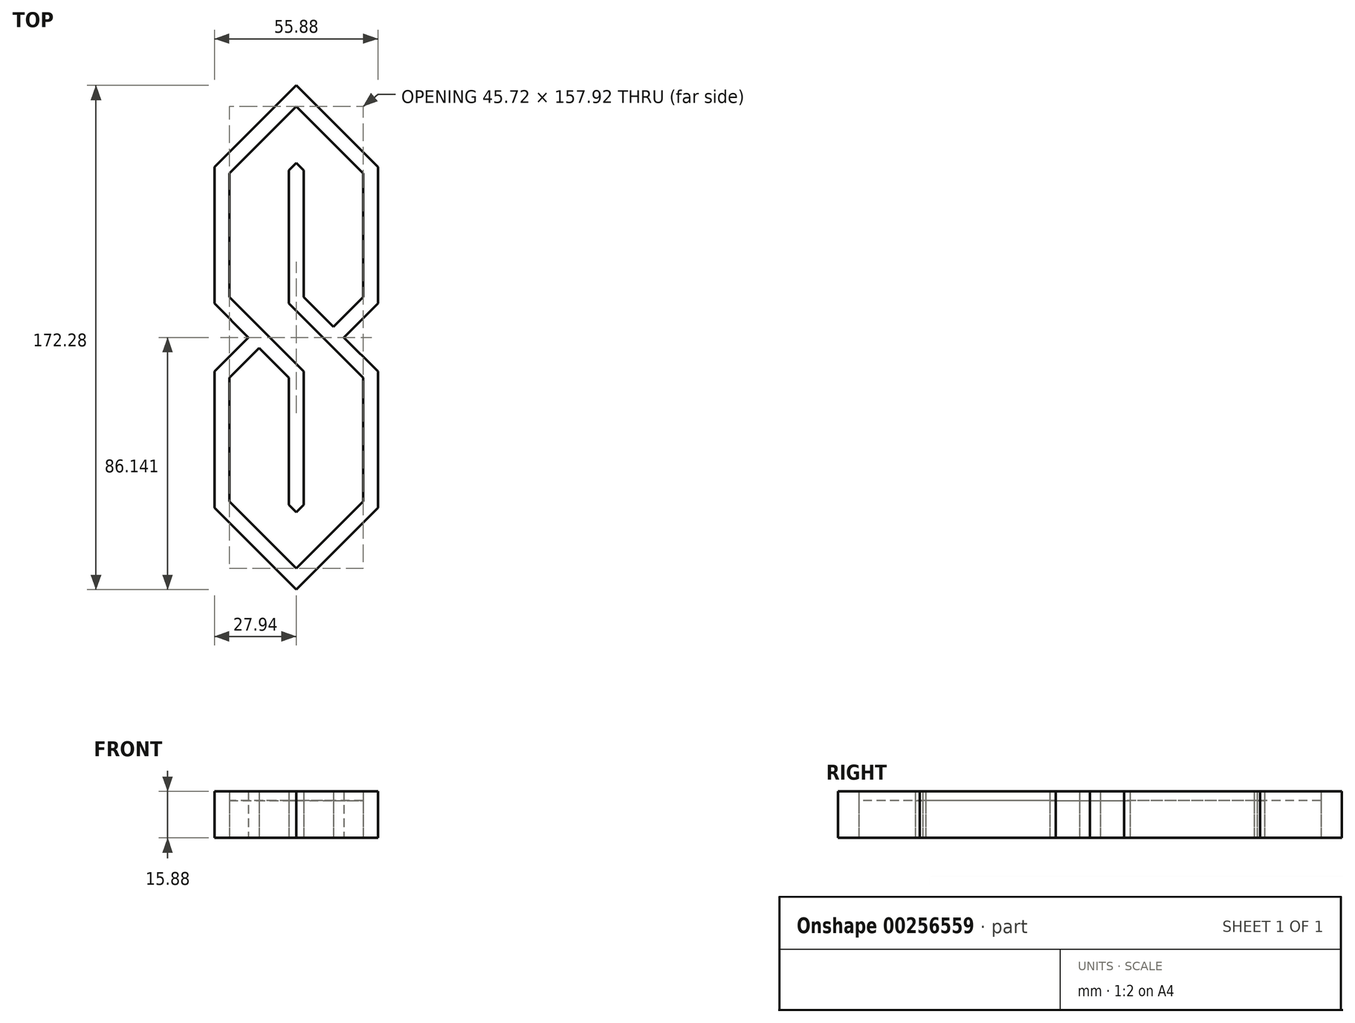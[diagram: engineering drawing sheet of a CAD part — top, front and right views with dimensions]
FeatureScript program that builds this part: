
annotation { "Feature Type Name" : "Feature", "Feature Type Description" : "" }
export const myFeature = defineFeature(function(context is Context, id is Id, definition is map)
    precondition{}
    {
        {
            var Q0;
            Q0=qCreatedBy(makeId("Top.planeOp"),FACE);
            var sketch = newSketch(context, id + "F0", { "sketchPlane" : qUnion([Q0])});
            skLineSegment(sketch, "E0", {"start": v(-29.25, 46.63) * mm, "end": v(-29.25, 2.18) * mm});
            skLineSegment(sketch, "E1", {"start": v(-3.85, 46.63) * mm, "end": v(-3.85, 2.18) * mm});
            skLineSegment(sketch, "E2", {"start": v(21.55, 46.63) * mm, "end": v(21.55, 2.18) * mm});
            skLineSegment(sketch, "E3", {"start": v(-29.25, -23.22) * mm, "end": v(-29.25, -67.67) * mm});
            skLineSegment(sketch, "E4", {"start": v(-3.85, -23.22) * mm, "end": v(-3.85, -67.67) * mm});
            skLineSegment(sketch, "E5", {"start": v(21.55, -23.22) * mm, "end": v(21.55, -67.67) * mm});
            skLineSegment(sketch, "E6", {"start": v(-3.85, -23.22) * mm, "end": v(-14.75, -12.32) * mm});
            skLineSegment(sketch, "E7", {"start": v(-29.25, 46.63) * mm, "end": v(-3.85, 72.03) * mm});
            skLineSegment(sketch, "E8", {"start": v(-3.85, 72.03) * mm, "end": v(21.55, 46.63) * mm});
            skLineSegment(sketch, "E9", {"start": v(-29.25, -67.67) * mm, "end": v(-3.85, -93.07) * mm});
            skLineSegment(sketch, "E10", {"start": v(-3.85, -93.07) * mm, "end": v(21.55, -67.67) * mm});
            skPoint(sketch, "E11", {"position": v(-16.55, -10.52) * mm});
            skPoint(sketch, "E12", {"position": v(8.85, -10.52) * mm});
            skPoint(sketch, "E13", {"position": v(-3.85, 2.18) * mm});
            skLineSegment(sketch, "E14", {"start": v(-29.25, -23.22) * mm, "end": v(-16.55, -10.52) * mm});
            skLineSegment(sketch, "E15", {"start": v(21.55, -23.22) * mm, "end": v(8.85, -10.52) * mm});
            skLineSegment(sketch, "E16", {"start": v(8.85, -10.52) * mm, "end": v(21.55, 2.18) * mm});
            skLineSegment(sketch, "E17.0", {"start": v(-26.7, 45.58) * mm, "end": v(-3.85, 68.44) * mm});
            skLineSegment(sketch, "E17.1", {"start": v(-26.7, 45.58) * mm, "end": v(-26.7, 3.23) * mm});
            skLineSegment(sketch, "E17.2", {"start": v(-1.3, -22.17) * mm, "end": v(-26.7, 3.23) * mm});
            skLineSegment(sketch, "E17.3", {"start": v(-1.3, -22.17) * mm, "end": v(-1.3, -67.67) * mm});
            skLineSegment(sketch, "E18.0", {"start": v(-26.7, -24.27) * mm, "end": v(-14.75, -12.32) * mm});
            skLineSegment(sketch, "E18.1", {"start": v(-26.7, -24.27) * mm, "end": v(-26.7, -66.62) * mm});
            skLineSegment(sketch, "E18.2", {"start": v(-26.7, -66.62) * mm, "end": v(-3.85, -89.48) * mm});
            skLineSegment(sketch, "E19.0", {"start": v(-6.39, 46.63) * mm, "end": v(-6.39, 1.13) * mm});
            skLineSegment(sketch, "E19.1", {"start": v(19.01, -24.27) * mm, "end": v(-6.39, 1.13) * mm});
            skLineSegment(sketch, "E19.2", {"start": v(19.01, -24.27) * mm, "end": v(19.01, -66.62) * mm});
            skLineSegment(sketch, "E19.3", {"start": v(-3.85, -89.48) * mm, "end": v(19.01, -66.62) * mm});
            skLineSegment(sketch, "E20.0", {"start": v(-3.85, 68.44) * mm, "end": v(19.01, 45.58) * mm});
            skLineSegment(sketch, "E20.1", {"start": v(19.01, 45.58) * mm, "end": v(19.01, 3.23) * mm});
            skLineSegment(sketch, "E20.2", {"start": v(7.05, -8.72) * mm, "end": v(19.01, 3.23) * mm});
            skLineSegment(sketch, "E21", {"start": v(-6.39, 46.63) * mm, "end": v(-3.85, 46.63) * mm});
            skLineSegment(sketch, "E22", {"start": v(-3.85, -67.67) * mm, "end": v(-1.3, -67.67) * mm});
            skLineSegment(sketch, "E23.trimOffspring", {"start": v(-16.55, -10.52) * mm, "end": v(-29.25, 2.18) * mm});
            skLineSegment(sketch, "E24.trimOffspring", {"start": v(7.05, -8.72) * mm, "end": v(-3.85, 2.18) * mm});
            skLineSegment(sketch, "E25.0", {"start": v(8.85, -6.93) * mm, "end": v(-1.3, 3.23) * mm});
            skLineSegment(sketch, "E25.1", {"start": v(-1.3, 46.63) * mm, "end": v(-1.3, 3.23) * mm});
            skLineSegment(sketch, "E26.0", {"start": v(-6.39, -24.27) * mm, "end": v(-6.39, -67.67) * mm});
            skLineSegment(sketch, "E26.1", {"start": v(-6.39, -24.27) * mm, "end": v(-16.55, -14.11) * mm});
            skLineSegment(sketch, "E27", {"start": v(-3.85, 72.03) * mm, "end": v(-3.85, 46.63) * mm, "construction": true});
            skPoint(sketch, "E28", {"position": v(-3.85, 59.33) * mm});
            skLineSegment(sketch, "E29", {"start": v(-3.85, 59.33) * mm, "end": v(-3.85, 68.44) * mm, "construction": true});
            skPoint(sketch, "E30", {"position": v(-3.85, 63.88) * mm});
            skLineSegment(sketch, "E31", {"start": v(-3.85, 46.63) * mm, "end": v(-1.3, 46.63) * mm});
            skLineSegment(sketch, "E32", {"start": v(-3.85, -67.67) * mm, "end": v(-6.39, -67.67) * mm});
            skLineSegment(sketch, "E33", {"start": v(-6.39, -67.67) * mm, "end": v(-3.85, -70.2) * mm});
            skLineSegment(sketch, "E34", {"start": v(-3.85, -70.2) * mm, "end": v(-1.3, -67.67) * mm});
            skLineSegment(sketch, "E35", {"start": v(-6.39, 46.63) * mm, "end": v(-3.85, 49.17) * mm});
            skLineSegment(sketch, "E36", {"start": v(-3.85, 49.17) * mm, "end": v(-1.3, 46.63) * mm});
            skLineSegment(sketch, "E37", {"start": v(19.01, -66.62) * mm, "end": v(-26.7, -66.62) * mm, "construction": true});
            skSolve(sketch);
        }
        {
            var Q0;
            Q0=makeQuery(id+"F0.imprint","IMPRINT",FACE,{"disambiguationData":[TD([[makeQuery(id+"F0.imprint","IMPRINT",EDGE,{"derivedFrom":sQuery(id+"F0.wireOp",EDGE,"E17.0")}),-1.0]])]});
            extrude(context, id + "F1", {"entities" : qUnion([Q0]), "depth" : 12.7 * mm, "offsetDistance" : 25.4 * mm});
        }
        {
            var Q0;
            Q0=qCreatedBy(makeId("Top.planeOp"),FACE);
            var sketch = newSketch(context, id + "F2", { "sketchPlane" : qUnion([Q0])});
            skLineSegment(sketch, "E38", {"start": v(-29.25, 46.63) * mm, "end": v(-29.25, 2.18) * mm});
            skLineSegment(sketch, "E39", {"start": v(-3.85, 46.63) * mm, "end": v(-3.85, 2.18) * mm});
            skLineSegment(sketch, "E40", {"start": v(21.55, 46.63) * mm, "end": v(21.55, 2.18) * mm});
            skLineSegment(sketch, "E41", {"start": v(-29.25, -23.22) * mm, "end": v(-29.25, -67.67) * mm});
            skLineSegment(sketch, "E42", {"start": v(-3.85, -23.22) * mm, "end": v(-3.85, -67.67) * mm});
            skLineSegment(sketch, "E43", {"start": v(21.55, -23.22) * mm, "end": v(21.55, -67.67) * mm});
            skLineSegment(sketch, "E44", {"start": v(-3.85, -23.22) * mm, "end": v(-14.75, -12.32) * mm});
            skLineSegment(sketch, "E45", {"start": v(-29.25, 46.63) * mm, "end": v(-3.85, 72.03) * mm});
            skLineSegment(sketch, "E46", {"start": v(-3.85, 72.03) * mm, "end": v(21.55, 46.63) * mm});
            skLineSegment(sketch, "E47", {"start": v(-29.25, -67.67) * mm, "end": v(-3.85, -93.07) * mm});
            skLineSegment(sketch, "E48", {"start": v(-3.85, -93.07) * mm, "end": v(21.55, -67.67) * mm});
            skPoint(sketch, "E49", {"position": v(-16.55, -10.52) * mm});
            skPoint(sketch, "E50", {"position": v(8.85, -10.52) * mm});
            skPoint(sketch, "E51", {"position": v(-3.85, 2.18) * mm});
            skLineSegment(sketch, "E52", {"start": v(-29.25, -23.22) * mm, "end": v(-16.55, -10.52) * mm});
            skLineSegment(sketch, "E53", {"start": v(21.55, -23.22) * mm, "end": v(8.85, -10.52) * mm});
            skLineSegment(sketch, "E54", {"start": v(8.85, -10.52) * mm, "end": v(21.55, 2.18) * mm});
            skLineSegment(sketch, "E55.0", {"start": v(-26.7, 45.58) * mm, "end": v(-3.85, 68.44) * mm});
            skLineSegment(sketch, "E55.1", {"start": v(-26.7, 45.58) * mm, "end": v(-26.7, 3.23) * mm});
            skLineSegment(sketch, "E55.2", {"start": v(-1.3, -22.17) * mm, "end": v(-26.7, 3.23) * mm});
            skLineSegment(sketch, "E55.3", {"start": v(-1.3, -22.17) * mm, "end": v(-1.3, -67.67) * mm});
            skLineSegment(sketch, "E56.0", {"start": v(-26.7, -24.27) * mm, "end": v(-14.75, -12.32) * mm});
            skLineSegment(sketch, "E56.1", {"start": v(-26.7, -24.27) * mm, "end": v(-26.7, -66.62) * mm});
            skLineSegment(sketch, "E56.2", {"start": v(-26.7, -66.62) * mm, "end": v(-3.85, -89.48) * mm});
            skLineSegment(sketch, "E57.0", {"start": v(-6.39, 46.63) * mm, "end": v(-6.39, 1.13) * mm});
            skLineSegment(sketch, "E57.1", {"start": v(19.01, -24.27) * mm, "end": v(-6.39, 1.13) * mm});
            skLineSegment(sketch, "E57.2", {"start": v(19.01, -24.27) * mm, "end": v(19.01, -66.62) * mm});
            skLineSegment(sketch, "E57.3", {"start": v(-3.85, -89.48) * mm, "end": v(19.01, -66.62) * mm});
            skLineSegment(sketch, "E58.0", {"start": v(-3.85, 68.44) * mm, "end": v(19.01, 45.58) * mm});
            skLineSegment(sketch, "E58.1", {"start": v(19.01, 45.58) * mm, "end": v(19.01, 3.23) * mm});
            skLineSegment(sketch, "E58.2", {"start": v(7.05, -8.72) * mm, "end": v(19.01, 3.23) * mm});
            skLineSegment(sketch, "E59", {"start": v(-6.39, 46.63) * mm, "end": v(-3.85, 46.63) * mm});
            skLineSegment(sketch, "E60", {"start": v(-3.85, -67.67) * mm, "end": v(-1.3, -67.67) * mm});
            skLineSegment(sketch, "E61.trimOffspring", {"start": v(-16.55, -10.52) * mm, "end": v(-29.25, 2.18) * mm});
            skLineSegment(sketch, "E62.trimOffspring", {"start": v(7.05, -8.72) * mm, "end": v(-3.85, 2.18) * mm});
            skLineSegment(sketch, "E63.0", {"start": v(8.85, -6.93) * mm, "end": v(-1.3, 3.23) * mm});
            skLineSegment(sketch, "E63.1", {"start": v(-1.3, 46.63) * mm, "end": v(-1.3, 3.23) * mm});
            skLineSegment(sketch, "E64.0", {"start": v(-6.39, -24.27) * mm, "end": v(-6.39, -67.67) * mm});
            skLineSegment(sketch, "E64.1", {"start": v(-6.39, -24.27) * mm, "end": v(-16.55, -14.11) * mm});
            skLineSegment(sketch, "E65", {"start": v(-3.85, 72.03) * mm, "end": v(-3.85, 46.63) * mm, "construction": true});
            skPoint(sketch, "E66", {"position": v(-3.85, 59.33) * mm});
            skLineSegment(sketch, "E67", {"start": v(-3.85, 59.33) * mm, "end": v(-3.85, 68.44) * mm, "construction": true});
            skPoint(sketch, "E68", {"position": v(-3.85, 63.88) * mm});
            skCircle(sketch, "E69", {"center": v(-3.85, 63.88) * mm, "radius": 2.11 * mm});
            skLineSegment(sketch, "E70", {"start": v(-3.85, 46.63) * mm, "end": v(-1.3, 46.63) * mm});
            skLineSegment(sketch, "E71", {"start": v(-3.85, -67.67) * mm, "end": v(-6.39, -67.67) * mm});
            skLineSegment(sketch, "E72", {"start": v(-6.39, -67.67) * mm, "end": v(-3.85, -70.2) * mm});
            skLineSegment(sketch, "E73", {"start": v(-3.85, -70.2) * mm, "end": v(-1.3, -67.67) * mm});
            skLineSegment(sketch, "E74", {"start": v(-6.39, 46.63) * mm, "end": v(-3.85, 49.17) * mm});
            skLineSegment(sketch, "E75", {"start": v(-3.85, 49.17) * mm, "end": v(-1.3, 46.63) * mm});
            skLineSegment(sketch, "E76", {"start": v(19.01, -66.62) * mm, "end": v(-26.7, -66.62) * mm, "construction": true});
            skPoint(sketch, "E77", {"position": v(-11.47, -19.2) * mm});
            skLineSegment(sketch, "E78.0", {"start": v(24.1, -22.17) * mm, "end": v(10.65, -8.72) * mm});
            skLineSegment(sketch, "E78.1", {"start": v(24.1, -22.17) * mm, "end": v(24.1, -68.72) * mm});
            skLineSegment(sketch, "E78.2", {"start": v(-31.79, -22.17) * mm, "end": v(-18.35, -8.72) * mm});
            skLineSegment(sketch, "E78.3", {"start": v(-31.79, -22.17) * mm, "end": v(-31.79, -68.72) * mm});
            skLineSegment(sketch, "E78.4", {"start": v(-31.79, -68.72) * mm, "end": v(-3.85, -96.66) * mm});
            skLineSegment(sketch, "E78.5", {"start": v(-3.85, -96.66) * mm, "end": v(24.1, -68.72) * mm});
            skLineSegment(sketch, "E79.0", {"start": v(10.65, -12.32) * mm, "end": v(24.1, 1.13) * mm});
            skLineSegment(sketch, "E79.1", {"start": v(24.1, 47.68) * mm, "end": v(24.1, 1.13) * mm});
            skLineSegment(sketch, "E79.2", {"start": v(-18.35, -12.32) * mm, "end": v(-31.79, 1.13) * mm});
            skLineSegment(sketch, "E79.3", {"start": v(-31.79, 47.68) * mm, "end": v(-31.79, 1.13) * mm});
            skLineSegment(sketch, "E79.4", {"start": v(-31.79, 47.68) * mm, "end": v(-3.85, 75.62) * mm});
            skLineSegment(sketch, "E79.5", {"start": v(-3.85, 75.62) * mm, "end": v(24.1, 47.68) * mm});
            skSolve(sketch);
        }
        {
            var Q0;
            Q0 = qSketchRegion(id + "F2", true);
            var Q1;
            Q1=makeQuery(id+"F2.imprint","IMPRINT",FACE,{"disambiguationData":[TD([[makeQuery(id+"F2.imprint","IMPRINT",EDGE,{"derivedFrom":sQuery(id+"F2.wireOp",EDGE,"E42")}),-1.0]])]});
            var Q2;
            Q2=makeQuery(id+"F2.imprint","IMPRINT",FACE,{"disambiguationData":[TD([[makeQuery(id+"F2.imprint","IMPRINT",EDGE,{"derivedFrom":sQuery(id+"F2.wireOp",EDGE,"E39")}),1.0]])]});
            var Q3;
            Q3=makeQuery(id+"F2.imprint","IMPRINT",FACE,{"disambiguationData":[TD([[makeQuery(id+"F2.imprint","IMPRINT",EDGE,{"derivedFrom":sQuery(id+"F2.wireOp",EDGE,"E59")}),1.0]])]});
            var Q4;
            Q4=makeQuery(id+"F2.imprint","IMPRINT",FACE,{"disambiguationData":[TD([[makeQuery(id+"F2.imprint","IMPRINT",EDGE,{"derivedFrom":sQuery(id+"F2.wireOp",EDGE,"E71")}),1.0]])]});
            var Q5;
            {var subQ15=sQuery(id+"F2.wireOp",EDGE,"E38");Q5=makeQuery(id+"F2.imprint","IMPRINT",FACE,{"disambiguationData":[TD([[makeQuery(id+"F2.imprint","IMPRINT",EDGE,{"derivedFrom":subQ15}),1.0]])]});}
            extrude(context, id + "F3", {"entities" : qUnion([Q0, Q1, Q2, Q3, Q4, Q5]), "depth" : 15.88 * mm, "offsetDistance" : 25.4 * mm});
        }
    });
